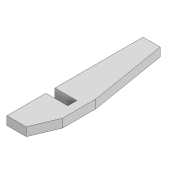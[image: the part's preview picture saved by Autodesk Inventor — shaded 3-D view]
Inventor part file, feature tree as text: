
AUTODESK INVENTOR PART (.ipt)
format: ipt  version: 2022 (Build 260153000, 153)  size: 94,720 bytes
history: native  units: mm
features: chamfer x2, extrude x1, sketch x1
ambient origin geometry x8: Origin, YZ Plane, XZ Plane, XY Plane, X Axis, Y Axis, Z Axis, Center Point
bodies: Solid1 (feature_tree)
feature tree (4):
  extrude  "Extrusion1"  Depth=31.8mm
  chamfer  "Chamfer1"  Distance=2.1mm
  chamfer  "Chamfer2"  Distance=5.1mm
  sketch  "Sketch1"  dims[d0=7.0mm d1=31.8mm d2=2.1mm d3=5.1mm d4=9.1mm d5=2.0mm d6=0.0mm d7=2.5mm d8=6.0mm d9=45.0deg d10=18.0mm d11=3.0mm d12=45.0deg]
